# Revit family: Kessel 93050 en
name_source: partatom
category: Sanitärinstallationen
revit_build: Autodesk Revit 2017 (Build: 20160225_1515(x64)
units: mm (PartAtom-declared; Revit-internal decimal feet)

## family parameters
Arbeitsebenenbasiert = Nein
Beim Laden mit Abzugskörper schneiden = Nein
Bemaßung runder Anschluss = Durchmesser verwenden
Gemeinsam genutzt = Nein
Immer vertikal = Ja
Raumberechnungspunkt = Nein
Teiletyp = Normal

## types (1)
- Kessel 93050 en
    <1.010.00.2> Number of the part of the guideline = 98
    <1.010.00.3> Issue date (month) of the guideline = 200601
    <1.010.00.4> Manufacturer name = Kessel
    <1.010.00.5> Revision date of the file = 20190227
    <1.800.00.3> BS number = 001002000001006003002002003001001001002???00300010???
    <1.800.00.4> Comment field = Fettabscheider EasyClean Modular NS 0,5, Standard, 2-teilig
    <1.810.00.3> Manufacturer’s reference number = 93050
    <1.810.00.4> DATANORM number = 93050
    <1.810.00.6> GTIN number = 4026092030899
    <1.960/3L.00.8> Link (URL) = http://www.kessel.de
    <98.100.00.4> Area of application = Abscheideranlage für Fette
    <98.110.00.4> Product series = Fettabscheider EasyClean Modular
    <98.200.00.3> Installation of the separators (DIN 19901) = Freiaufstellung
    <98.250.00.3> Disposal variant = Standard
    <98.260.00.3> Sludge trap content (liters) = 50
    <98.300.00.3> Separator content (liters) = 42
    <98.350.00.3> Fat storage (liters) = 30
    <98.360.00.3> Total volume (liters) = 92
    <98.400.00.3> Layer thickness measurement (SonicControl) = nein
    <98.450.00.3> Inlet nominal diameter (DN) = 40
    <98.460.00.3> Outlet nominal diameter (DN) = 40
    <98.500.00.3> Nominal size (NS) = 0,5
    <98.700.00.4> Product name = Fettabscheider EasyClean Modular NS 0,5, Standard, 2-teilig
    CONNECTOR0_DIAMETER_dX_0r = 0 mm  [stored 0 ft]
    CONNECTOR0_dX_00 = 555 mm
    CONNECTOR0_dX_01 = 469 mm
    CONNECTOR0_ref_dX = 469 mm
    CONNECTOR0_ref_dZ = 550 mm  [stored 1.80446 ft]
    CONNECTOR1_DIAMETER_dX_0r = 0 mm  [stored 0 ft]
    CONNECTOR1_dX_00 = 476 mm
    CONNECTOR1_dX_01 = 562 mm
    CONNECTOR1_ref_dX = 476 mm
    CONNECTOR1_ref_dZ = 550 mm  [stored 1.80446 ft]
    Hersteller = Kessel
    Modell = 93050
    URL = www.kessel.de

note: [stored X ft] marks values corroborated as IEEE doubles in the binary element streams (Revit-internal decimal feet)

## geometry (parser evidence)
native form markers: Sweep x2
no freeform markers — native parametric forms only
